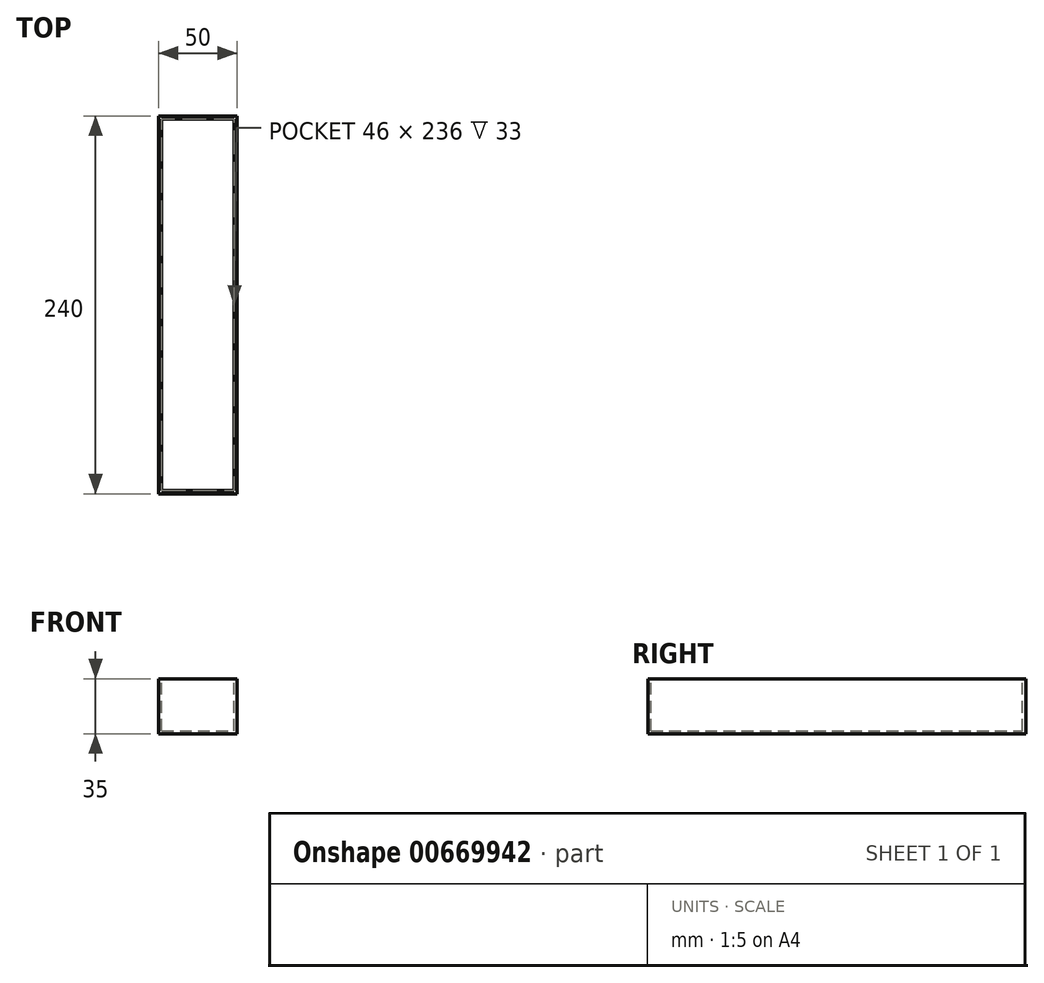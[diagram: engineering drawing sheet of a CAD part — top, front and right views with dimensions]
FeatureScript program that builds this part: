
annotation { "Feature Type Name" : "Feature", "Feature Type Description" : "" }
export const myFeature = defineFeature(function(context is Context, id is Id, definition is map)
    precondition{}
    {
        {
            var Q0;
            Q0=qCreatedBy(makeId("Front.planeOp"),FACE);
            var sketch = newSketch(context, id + "F0", { "sketchPlane" : qUnion([Q0])});
            skLineSegment(sketch, "E0.bottom", {"start": v(0, 0) * mm, "end": v(50, 0) * mm});
            skLineSegment(sketch, "E0.top", {"start": v(0, 35) * mm, "end": v(50, 35) * mm});
            skLineSegment(sketch, "E0.left", {"start": v(0, 0) * mm, "end": v(0, 35) * mm});
            skLineSegment(sketch, "E0.right", {"start": v(50, 0) * mm, "end": v(50, 35) * mm});
            skSolve(sketch);
        }
        {
            var Q0;
            Q0=makeQuery(id+"F0.imprint","IMPRINT",FACE,{"disambiguationData":[TD([[makeQuery(id+"F0.imprint","IMPRINT",EDGE,{"derivedFrom":sQuery(id+"F0.wireOp",EDGE,"E0.bottom")}),1.0]])]});
            extrude(context, id + "F1", {"entities" : qUnion([Q0]), "depth" : 240 * mm, "offsetDistance" : 25 * mm});
        }
        {
            var Q0;
            Q0=makeQuery(id+"F1.opExtrude","SWEPT_FACE",FACE,{"disambiguationData":[OSD([sQuery(id+"F0.wireOp",EDGE,"E0.top")])]});
            shell(context, id + "F2", {"entities" : qUnion([Q0]), "thickness" : 2 * mm});
        }
    });
